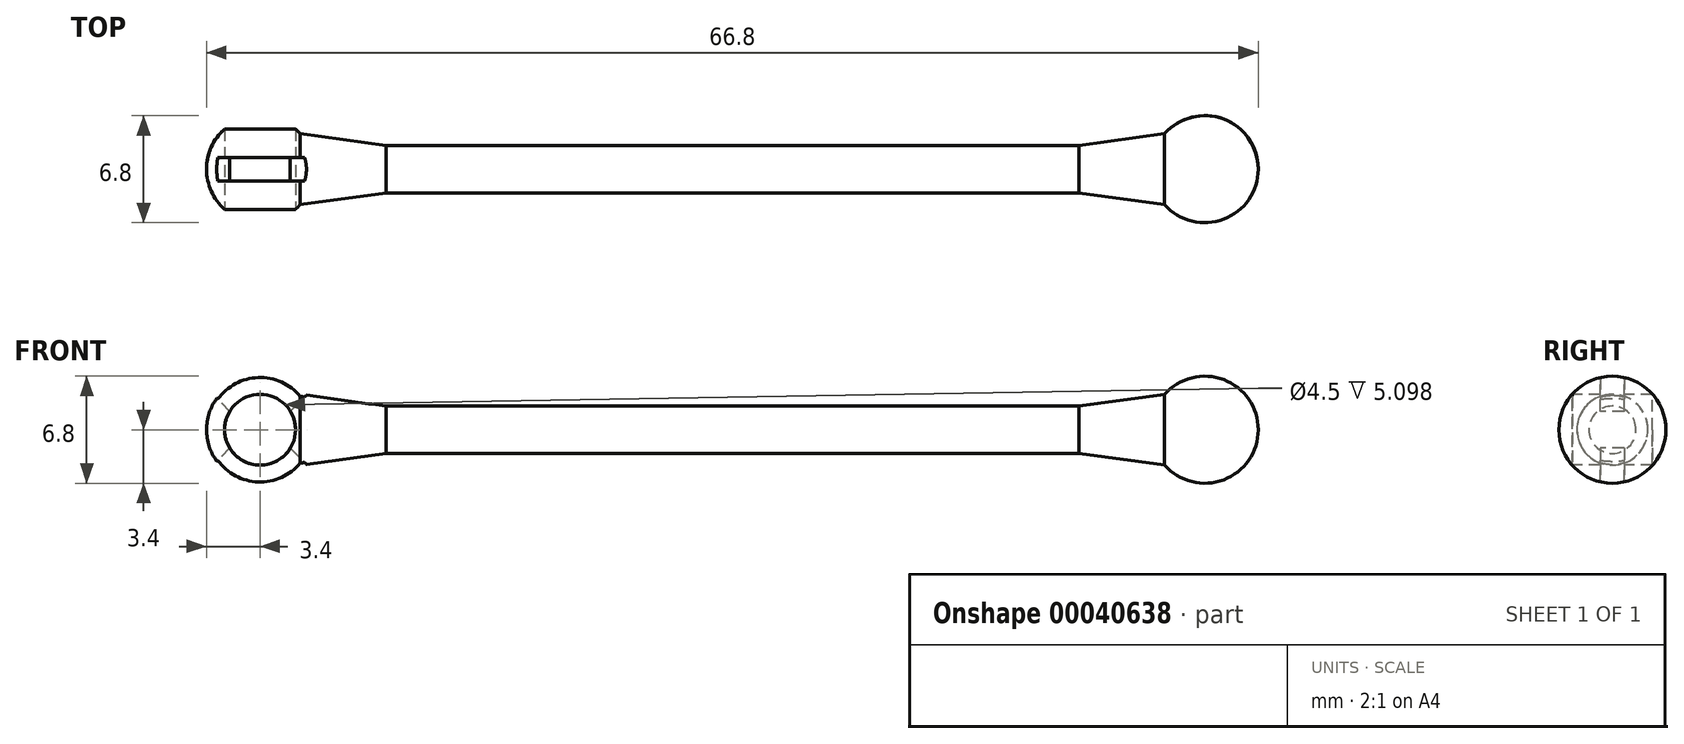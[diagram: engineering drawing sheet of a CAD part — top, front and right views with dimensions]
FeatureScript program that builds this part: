
annotation { "Feature Type Name" : "Feature", "Feature Type Description" : "" }
export const myFeature = defineFeature(function(context is Context, id is Id, definition is map)
    precondition{}
    {
        {
            var Q0;
            Q0=qCreatedBy(makeId("Top.planeOp"),FACE);
            var sketch = newSketch(context, id + "F0", { "sketchPlane" : qUnion([Q0])});
            skLineSegment(sketch, "E0", {"start": v(-50, 0) * mm, "end": v(50, 0) * mm, "construction": true});
            skLineSegment(sketch, "E1", {"start": v(0, 50) * mm, "end": v(0, -50) * mm, "construction": true});
            skSolve(sketch);
        }
        {
            var Q0;
            Q0=qCreatedBy(makeId("Front.planeOp"),FACE);
            var sketch = newSketch(context, id + "F1", { "sketchPlane" : qUnion([Q0])});
            skLineSegment(sketch, "E2", {"start": v(0, 50) * mm, "end": v(0, -50) * mm, "construction": true});
            skSolve(sketch);
        }
        {
            var Q0;
            Q0=qCreatedBy(makeId("Front.planeOp"),FACE);
            var sketch = newSketch(context, id + "F2", { "sketchPlane" : qUnion([Q0])});
            skLineSegment(sketch, "E3.bottom", {"start": v(-30, 0) * mm, "end": v(0, 0) * mm});
            skLineSegment(sketch, "E3.top", {"start": v(-30, 1.5) * mm, "end": v(0, 1.5) * mm});
            skLineSegment(sketch, "E3.left", {"start": v(-30, 0) * mm, "end": v(-30, 1.5) * mm});
            skLineSegment(sketch, "E3.right", {"start": v(0, 0) * mm, "end": v(0, 1.5) * mm});
            skLineSegment(sketch, "E4.MirrorCS", {"start": v(30, 0) * mm, "end": v(30, 1.5) * mm, "construction": true});
            skLineSegment(sketch, "E5.0", {"start": v(-50, 0) * mm, "end": v(50, 0) * mm, "construction": true});
            skSolve(sketch);
        }
        {
            var Q0;
            Q0=qSketchRegion(id+"F2",true);
            var Q1;
            Q1=sQuery(id+"F0.wireOp",EDGE,"E0");
            revolve(context, id + "F3", {"entities" : qUnion([Q0]), "axis" : qUnion([Q1]), "revolveType" : RevolveType.SYMMETRIC, "angle" : 180 * degree});
        }
        {
            var Q0;
            Q0=qCreatedBy(makeId("Front.planeOp"),FACE);
            var sketch = newSketch(context, id + "F4", { "sketchPlane" : qUnion([Q0])});
            skCircle(sketch, "E6", {"center": v(-30, 0) * mm, "radius": 3.4 * mm, "construction": true});
            skArc(sketch, "E7", {"start": v(-26.6, 0) * mm, "mid": v(-30, 3.4) * mm, "end": v(-33.4, 0) * mm});
            skLineSegment(sketch, "E8", {"start": v(-33.4, 0) * mm, "end": v(-26.6, 0) * mm});
            skSolve(sketch);
        }
        {
            var Q0;
            Q0=qSketchRegion(id+"F4",true);
            var Q1;
            Q1=sQuery(id+"F0.wireOp",EDGE,"E0");
            revolve(context, id + "F5", {"operationType" : NewBodyOperationType.ADD, "entities" : qUnion([Q0]), "axis" : qUnion([Q1]), "revolveType" : RevolveType.SYMMETRIC, "angle" : 180 * degree});
        }
        {
            var Q0;
            Q0=qCreatedBy(makeId("Front.planeOp"),FACE);
            var sketch = newSketch(context, id + "F6", { "sketchPlane" : qUnion([Q0])});
            skLineSegment(sketch, "E9", {"start": v(-30, 2.25) * mm, "end": v(-27.45, 2.25) * mm});
            skLineSegment(sketch, "E10", {"start": v(-27.45, 2.25) * mm, "end": v(-22, 1.5) * mm});
            skLineSegment(sketch, "E11", {"start": v(-22, 1.5) * mm, "end": v(-22, 0) * mm});
            skLineSegment(sketch, "E12", {"start": v(-22, 0) * mm, "end": v(-30, 0) * mm});
            skLineSegment(sketch, "E13", {"start": v(-30, 2.25) * mm, "end": v(-30, 0) * mm});
            skLineSegment(sketch, "E14.0", {"start": v(-50, 0) * mm, "end": v(50, 0) * mm, "construction": true});
            skSolve(sketch);
        }
        {
            var Q0;
            Q0=makeQuery(id+"F6.imprint","IMPRINT",FACE,{"disambiguationData":[TD([[makeQuery(id+"F6.imprint","IMPRINT",EDGE,{"derivedFrom":sQuery(id+"F6.wireOp",EDGE,"E10")}),-1.0]])]});
            var Q1;
            Q1=sQuery(id+"F0.wireOp",EDGE,"E0");
            revolve(context, id + "F7", {"operationType" : NewBodyOperationType.ADD, "entities" : qUnion([Q0]), "axis" : qUnion([Q1]), "revolveType" : RevolveType.SYMMETRIC, "angle" : 180 * degree});
        }
        {
            var Q0;
            Q0=makeQuery(id+"F3.opRevolve","SWEPT_BODY",BODY,{"disambiguationData":[OSD([sQuery(id+"F2.wireOp",EDGE,"E3.bottom"),sQuery(id+"F2.wireOp",EDGE,"E3.left"),sQuery(id+"F2.wireOp",EDGE,"E3.right"),sQuery(id+"F2.wireOp",EDGE,"E3.top")])]});
            var Q1;
            Q1=qCreatedBy(makeId("Right.planeOp"),FACE);
            mirror(context, id + "F8", {"operationType" : NewBodyOperationType.ADD, "entities" : qUnion([Q0]), "mirrorPlane" : qUnion([Q1])});
        }
        {
            var Q0;
            Q0=qCreatedBy(makeId("Front.planeOp"),FACE);
            var sketch = newSketch(context, id + "F9", { "sketchPlane" : qUnion([Q0])});
            skCircle(sketch, "E15", {"center": v(-30, 0) * mm, "radius": 2.25 * mm});
            skSolve(sketch);
        }
        {
            var Q0;
            Q0=makeQuery(id+"F9.imprint","IMPRINT",FACE,{"disambiguationData":[TD([[makeQuery(id+"F9.imprint","IMPRINT",EDGE,{"derivedFrom":sQuery(id+"F9.wireOp",EDGE,"E15")}),1.0]])]});
            extrude(context, id + "F10", {"entities" : qUnion([Q0]), "operationType" : NewBodyOperationType.REMOVE, "endBound" : BoundingType.THROUGH_ALL, "oppositeDirection" : true, "depth" : 25 * mm, "hasSecondDirection" : true, "secondDirectionBound" : SecondDirectionBoundingType.THROUGH_ALL, "secondDirectionOppositeDirection" : false, "secondDirectionDepth" : 25 * mm});
        }
        {
            var Q0;
            Q0=qCreatedBy(makeId("Front.planeOp"),FACE);
            var sketch = newSketch(context, id + "F11", { "sketchPlane" : qUnion([Q0])});
            skLineSegment(sketch, "E16", {"start": v(-30.75, 0) * mm, "end": v(-34.15, 3.4) * mm});
            skLineSegment(sketch, "E17.MirrorCS", {"start": v(-29.25, 0) * mm, "end": v(-25.85, 3.4) * mm});
            skLineSegment(sketch, "E18", {"start": v(-30.75, 0) * mm, "end": v(-29.25, 0) * mm});
            skLineSegment(sketch, "E19", {"start": v(-34.15, 3.4) * mm, "end": v(-25.85, 3.4) * mm});
            skSolve(sketch);
        }
        {
            var Q0;
            Q0=makeQuery(id+"F11.imprint","IMPRINT",FACE,{"disambiguationData":[TD([[makeQuery(id+"F11.imprint","IMPRINT",EDGE,{"derivedFrom":sQuery(id+"F11.wireOp",EDGE,"E16")}),-1.0]])]});
            extrude(context, id + "F12", {"entities" : qUnion([Q0]), "operationType" : NewBodyOperationType.REMOVE, "endBound" : BoundingType.SYMMETRIC, "depth" : 1.5 * mm});
        }
        {
            var Q0;
            Q0=makeQuery(id+"F3.opRevolve","SWEPT_BODY",BODY,{"disambiguationData":[OSD([sQuery(id+"F2.wireOp",EDGE,"E3.bottom"),sQuery(id+"F2.wireOp",EDGE,"E3.left"),sQuery(id+"F2.wireOp",EDGE,"E3.right"),sQuery(id+"F2.wireOp",EDGE,"E3.top")])]});
            var Q1;
            Q1=qCreatedBy(makeId("Top.planeOp"),FACE);
            mirror(context, id + "F13", {"operationType" : NewBodyOperationType.ADD, "entities" : qUnion([Q0]), "mirrorPlane" : qUnion([Q1])});
        }
    });
